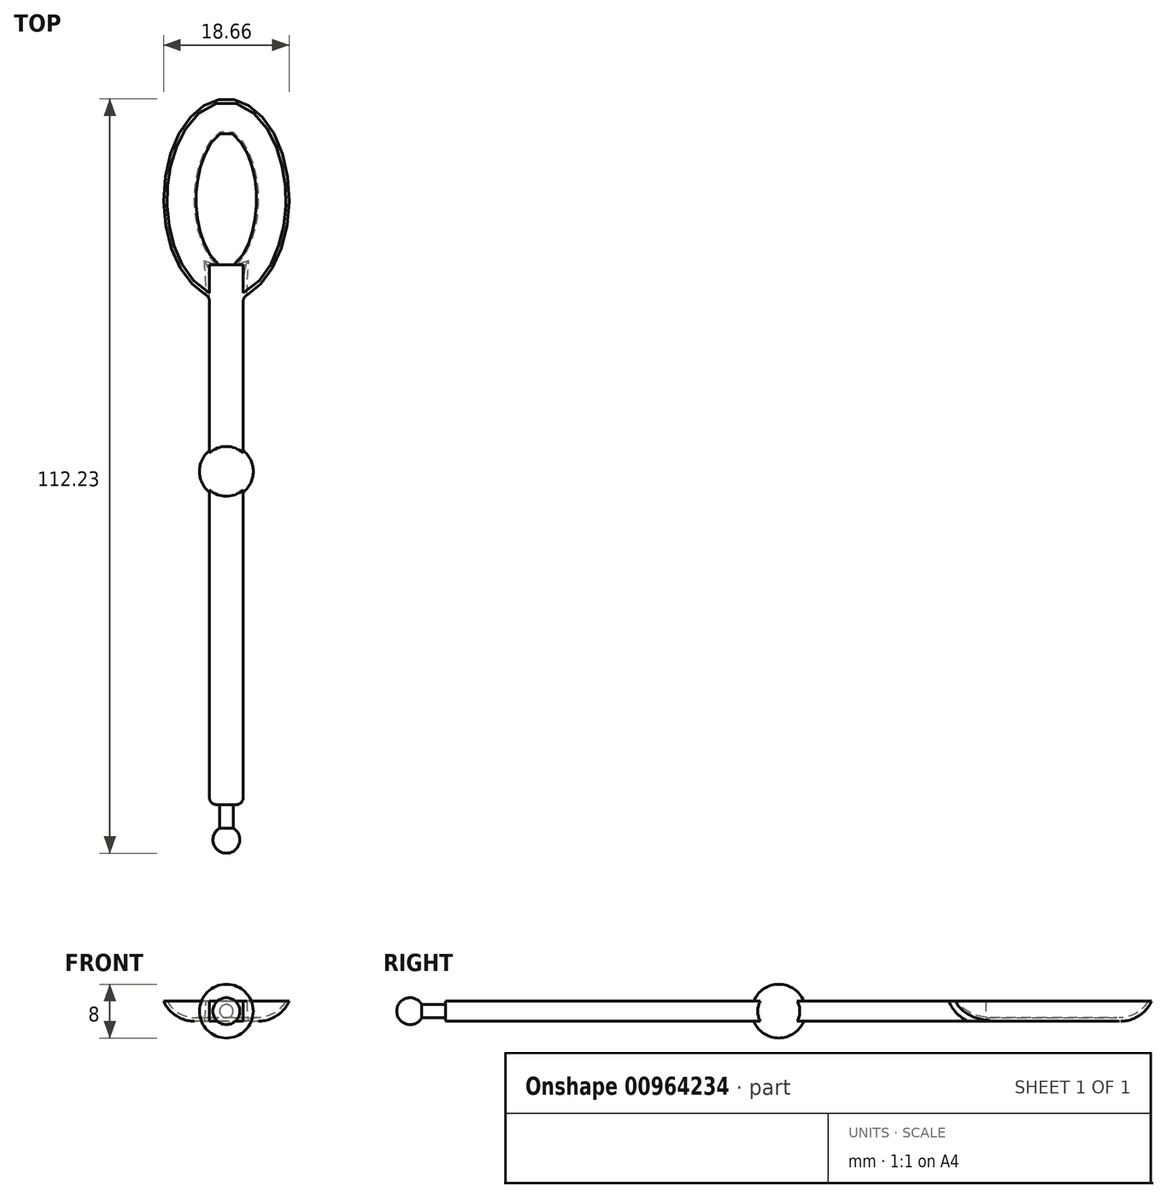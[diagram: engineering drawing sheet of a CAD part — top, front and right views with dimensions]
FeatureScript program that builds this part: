
annotation { "Feature Type Name" : "Feature", "Feature Type Description" : "" }
export const myFeature = defineFeature(function(context is Context, id is Id, definition is map)
    precondition{}
    {
        {
            var Q0;
            Q0=qCreatedBy(makeId("Top.planeOp"),FACE);
            var sketch = newSketch(context, id + "F0", { "sketchPlane" : qUnion([Q0])});
            skPoint(sketch, "E0.middle", {"position": v(0, 0) * mm});
            skEllipse(sketch, "E1", {"center": v(0, 0) * mm, "majorRadius": 15 * mm, "minorRadius": 9.33 * mm, "majorAxis": v(0, 1)});
            skSolve(sketch);
        }
        {
            var Q0;
            Q0=makeQuery(id+"F0.imprint","IMPRINT",FACE,{"disambiguationData":[TD([[makeQuery(id+"F0.imprint","IMPRINT",EDGE,{"derivedFrom":sQuery(id+"F0.wireOp",EDGE,"E1")}),1.0]])]});
            var Q1;
            Q1=sQuery(id+"F0.wireOp",EDGE,"E0.left");
            extrude(context, id + "F1", {"entities" : qUnion([Q0]), "surfaceEntities" : qUnion([Q1]), "endBound" : BoundingType.SYMMETRIC, "depth" : 3 * mm, "offsetDistance" : 25 * mm});
        }
        {
            var Q0;
            Q0=makeQuery(id+"F1.opExtrude","CAP_FACE",FACE,{"disambiguationData":[OSD([sQuery(id+"F0.wireOp",EDGE,"E1")])],"isStart":false});
            var Q1;
            Q1=makeQuery(id+"F1.opExtrude","SWEPT_BODY",BODY,{"disambiguationData":[OSD([sQuery(id+"F0.wireOp",EDGE,"779488db-b665-45dc-9fcb-b5043c60f5eb"),sQuery(id+"F0.wireOp",EDGE,"E0.top"),sQuery(id+"F0.wireOp",EDGE,"E0.left"),sQuery(id+"F0.wireOp",EDGE,"E0.right"),sQuery(id+"F0.wireOp",EDGE,"b7c9cc2e-7b79-4f78-8673-42c8bb0c6bb0.filletArc"),sQuery(id+"F0.wireOp",EDGE,"2931a396-7cc0-4279-9e17-49047f8ccdf3.filletArc"),sQuery(id+"F0.wireOp",EDGE,"6ae53be5-ede5-4ddb-84d4-b33327a7e2b9.filletArc"),sQuery(id+"F0.wireOp",EDGE,"a07cc649-7d3c-463b-b7a9-0f93a22f079b.filletArc")])]});
            shell(context, id + "F2", {"entities" : qUnion([Q0]), "parts" : qUnion([Q1]), "thickness" : 0.5 * mm});
        }
        {
            var Q0;
            {var subQ0=sQuery(id+"F0.wireOp",EDGE,"E1");Q0=makeQuery(id+"F2.opShell","OFFSET_EDGE",EDGE,{"disambiguationData":[OSD([subQ0]),TDD([makeQuery(id+"F1.opExtrude","CAP_EDGE",EDGE,{"disambiguationData":[OSD([subQ0])],"isStart":true})])]});}
            var Q1;
            Q1=makeQuery(id+"F1.opExtrude","CAP_EDGE",EDGE,{"disambiguationData":[OSD([sQuery(id+"F0.wireOp",EDGE,"E1")])],"isStart":true});
            fillet(context, id + "F3", {"entities" : qUnion([Q0, Q1]), "radius" : 5 * mm, "tangentPropagation" : true, "allowEdgeOverflow" : false});
        }
        {
            var Q0;
            Q0=qCreatedBy(makeId("Top.planeOp"),FACE);
            var sketch = newSketch(context, id + "F4", { "sketchPlane" : qUnion([Q0])});
            skLineSegment(sketch, "E2.top", {"start": v(-1.5, -90) * mm, "end": v(1.5, -90) * mm});
            skLineSegment(sketch, "E2.left", {"start": v(-2.5, -9.67) * mm, "end": v(-2.5, -89) * mm});
            skLineSegment(sketch, "E2.right", {"start": v(2.5, -9.67) * mm, "end": v(2.5, -89) * mm});
            skPoint(sketch, "E3.visualSharp", {"position": v(2.5, -90) * mm});
            skArc(sketch, "E3.filletArc", {"start": v(1.5, -90) * mm, "mid": v(2.2, -89.7) * mm, "end": v(2.5, -89) * mm});
            skPoint(sketch, "E4.visualSharp", {"position": v(-2.5, -90) * mm});
            skArc(sketch, "E4.filletArc", {"start": v(-2.5, -89) * mm, "mid": v(-2.2, -89.7) * mm, "end": v(-1.5, -90) * mm});
            skLineSegment(sketch, "E5", {"start": v(-2.5, -9.67) * mm, "end": v(2.5, -9.67) * mm});
            skSolve(sketch);
        }
        {
            var Q0;
            Q0=makeQuery(id+"F4.imprint","IMPRINT",FACE,{"disambiguationData":[TD([[makeQuery(id+"F4.imprint","IMPRINT",EDGE,{"derivedFrom":sQuery(id+"F4.wireOp",EDGE,"E2.top")}),1.0]])]});
            extrude(context, id + "F5", {"entities" : qUnion([Q0]), "operationType" : NewBodyOperationType.ADD, "endBound" : BoundingType.SYMMETRIC, "depth" : 3 * mm, "offsetDistance" : 25 * mm});
        }
        {
            var Q0;
            {var subQ0=sQuery(id+"F0.wireOp",EDGE,"E1");Q0=makeQuery(id+"F5.boolean.opBoolean","INTERSECT",EDGE,{"derivedFrom":[makeQuery(id+"F3.opFillet","BLEND_FACE",FACE,{"disambiguationData":[OSD([subQ0]),TDD([makeQuery(id+"F1.opExtrude","CAP_EDGE",EDGE,{"disambiguationData":[OSD([subQ0])],"isStart":true})])]}),makeQuery(id+"F5.opExtrude","SWEPT_FACE",FACE,{"disambiguationData":[OSD([sQuery(id+"F4.wireOp",EDGE,"E2.left")])]})]});}
            var Q1;
            {var subQ0=sQuery(id+"F0.wireOp",EDGE,"E1");Q1=makeQuery(id+"F5.boolean.opBoolean","INTERSECT",EDGE,{"derivedFrom":[makeQuery(id+"F3.opFillet","BLEND_FACE",FACE,{"disambiguationData":[OSD([subQ0]),TDD([makeQuery(id+"F1.opExtrude","CAP_EDGE",EDGE,{"disambiguationData":[OSD([subQ0])],"isStart":true})])]}),makeQuery(id+"F5.opExtrude","SWEPT_FACE",FACE,{"disambiguationData":[OSD([sQuery(id+"F4.wireOp",EDGE,"E2.right")])]})]});}
            var Q2;
            {var subQ0=sQuery(id+"F0.wireOp",EDGE,"E1");Q2=makeQuery(id+"F5.boolean.opBoolean","INTERSECT",EDGE,{"disambiguationData":[OD(0.0)],"derivedFrom":[makeQuery(id+"F3.opFillet","BLEND_FACE",FACE,{"disambiguationData":[OSD([subQ0]),TDD([makeQuery(id+"F1.opExtrude","CAP_EDGE",EDGE,{"disambiguationData":[OSD([subQ0])],"isStart":true})])]}),makeQuery(id+"F5.opExtrude","SWEPT_FACE",FACE,{"disambiguationData":[OSD([sQuery(id+"F4.wireOp",EDGE,"E5")])]})]});}
            var Q3;
            {var subQ0=sQuery(id+"F0.wireOp",EDGE,"E1");Q3=makeQuery(id+"F5.boolean.opBoolean","INTERSECT",EDGE,{"disambiguationData":[OD(1.0)],"derivedFrom":[makeQuery(id+"F3.opFillet","BLEND_FACE",FACE,{"disambiguationData":[OSD([subQ0]),TDD([makeQuery(id+"F1.opExtrude","CAP_EDGE",EDGE,{"disambiguationData":[OSD([subQ0])],"isStart":true})])]}),makeQuery(id+"F5.opExtrude","SWEPT_FACE",FACE,{"disambiguationData":[OSD([sQuery(id+"F4.wireOp",EDGE,"E5")])]})]});}
            fillet(context, id + "F6", {"entities" : qUnion([Q0, Q1, Q2, Q3]), "radius" : 1 * mm, "tangentPropagation" : true, "allowEdgeOverflow" : false});
        }
        {
            var Q0;
            Q0=qCreatedBy(makeId("Top.planeOp"),FACE);
            var sketch = newSketch(context, id + "F7", { "sketchPlane" : qUnion([Q0])});
            skArc(sketch, "E6", {"start": v(0, -44.43) * mm, "mid": v(4, -40.43) * mm, "end": v(0, -36.43) * mm});
            skLineSegment(sketch, "E7", {"start": v(0, -36.43) * mm, "end": v(0, -44.43) * mm});
            skSolve(sketch);
        }
        {
            var Q0;
            Q0=makeQuery(id+"F7.imprint","IMPRINT",FACE,{"disambiguationData":[TD([[makeQuery(id+"F7.imprint","IMPRINT",EDGE,{"derivedFrom":sQuery(id+"F7.wireOp",EDGE,"E6")}),1.0]])]});
            var Q1;
            {var subQ0=sQuery(id+"F7.wireOp",EDGE,"E6");var subQ1=sQuery(id+"F4.wireOp",EDGE,"E2.right");var subQ3=sQuery(id+"F4.wireOp",EDGE,"E3.filletArc");var subQ4=makeQuery(id+"F5.boolean.opBoolean","SPLIT",EDGE,{"disambiguationData":[TD([makeQuery(id+"F5.opExtrude","SWEPT_FACE",FACE,{"disambiguationData":[OSD([subQ3])]})])],"derivedFrom":makeQuery(id+"F5.opExtrude","CAP_EDGE",EDGE,{"disambiguationData":[OSD([subQ1])],"isStart":false})});var subQ5=makeQuery(id+"F7.imprint","INTERSECT",VERTEX,{"disambiguationData":[OD(0.0)],"derivedFrom":[subQ4,subQ0]});Q1=makeQuery(id+"F7.imprint","IMPRINT",FACE,{"disambiguationData":[TD([[makeQuery(id+"F7.imprint","IMPRINT",EDGE,{"disambiguationData":[TD([[subQ5,-1.0]])],"derivedFrom":subQ0}),1.0]])]});}
            var Q2;
            Q2=sQuery(id+"F7.wireOp",EDGE,"E7");
            revolve(context, id + "F8", {"operationType" : NewBodyOperationType.ADD, "surfaceOperationType" : NewSurfaceOperationType.NEW, "entities" : qUnion([Q0, Q1]), "axis" : qUnion([Q2]), "revolveType" : RevolveType.FULL});
        }
        {
            var Q0;
            Q0=qCreatedBy(makeId("Top.planeOp"),FACE);
            var sketch = newSketch(context, id + "F9", { "sketchPlane" : qUnion([Q0])});
            skLineSegment(sketch, "E8.top", {"start": v(0, -87.5) * mm, "end": v(1, -87.5) * mm});
            skLineSegment(sketch, "E8.right", {"start": v(1, -93.5) * mm, "end": v(1, -87.5) * mm});
            skPoint(sketch, "E8.middle", {"position": v(0, -91.37) * mm});
            skArc(sketch, "E9", {"start": v(0, -97.23) * mm, "mid": v(1.93, -95.75) * mm, "end": v(1, -93.5) * mm});
            skPoint(sketch, "E10.orphan", {"position": v(1, -95.23) * mm});
            skPoint(sketch, "E11.orphan", {"position": v(-1, -95.23) * mm});
            skLineSegment(sketch, "E12", {"start": v(0, -87.5) * mm, "end": v(0, -97.23) * mm});
            skPoint(sketch, "E8.left.start.orphan", {"position": v(-1, -93.5) * mm});
            skPoint(sketch, "E13.orphan", {"position": v(-1, -87.5) * mm});
            skSolve(sketch);
        }
        {
            var Q0;
            Q0=makeQuery(id+"F9.imprint","IMPRINT",FACE,{"disambiguationData":[TD([[makeQuery(id+"F9.imprint","IMPRINT",EDGE,{"derivedFrom":sQuery(id+"F9.wireOp",EDGE,"E8.top")}),-1.0]])]});
            var Q1;
            Q1=sQuery(id+"F9.wireOp",EDGE,"E12");
            revolve(context, id + "F10", {"operationType" : NewBodyOperationType.ADD, "surfaceOperationType" : NewSurfaceOperationType.NEW, "entities" : qUnion([Q0]), "axis" : qUnion([Q1]), "revolveType" : RevolveType.FULL});
        }
    });
